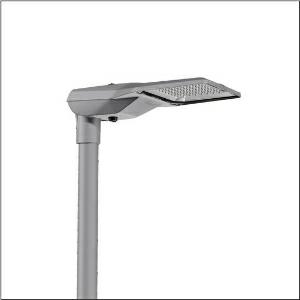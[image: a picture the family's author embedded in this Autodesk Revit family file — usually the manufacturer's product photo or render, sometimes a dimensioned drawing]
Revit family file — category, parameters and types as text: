
# Revit family: streetlight_sl_21_midi___p0_5a_5xe3v33t08nb_a5b7
name_source: partatom
category: Lighting Fixtures
units: mm (PartAtom-declared; Revit-internal decimal feet)

## family parameters
Cut with Voids When Loaded = No
Host = Face
Light Source = No
Part Type = Normal
Room Calculation Point = No
Round Connector Dimension = Use Diameter
Shared = No

## types (1)
- --- (1 x LED, 22310 lm, 151.2 W, 3000K)
    Apparent Load = 151 VA
    CIE Flux Codes = 37 73 96 100 100
    Color Rendering = 70
    Color Temperature = 3000K
    Default Elevation = 1800 mm
    Description = Streetlight SL 21 midi, mast luminaire, primary light control with lens, of PMMA, primary optical cover: cover, of toughened safety glass, transparent, light distribution: P0.5a, light emission: direct distribution, primary light characteristic: asymmetric, installation type: post-top, side-entry, LED, High Power LED, rated luminous flux: 22.310lm, luminous efficacy: 148lm/W, light colour: 730, colour temperature: 3000K, control gear: D4i, control: overheat protection, constant luminous flux control, time-dependent luminous flux control, flexible luminous flux parameterisation, pre-setting: logarithmic dimming characteristic, mains connection: 230..240V, AC, 50/60Hz, start of lifetime: 151W, end of service life: 157W, reduction: 70W, luminaire housing, of diecast aluminium, powder-coated, Siteco® metallic grey (DB 702S), corrosivity category C5 mid according to DIN EN ISO 12944, multi-level sealing system, sealing non-destructively replaceable, inclination adjustable: 0°, 5°, 10°, 15°, please order mast flange separately, length: 644mm, width: 335mm, height: 110mm, mast flange for spigot size: 42mm (side-entry): 5XC10008XM4, 60/48mm (side-entry/post-top): 5XC10108XM2, 76/60mm (side-entry/post-top): 5XC10108XM1, mounting height: 4..8m, Smart Interface below and above, protection rating (complete): IP66, insulation class (complete): insulation class II (safety insulation), certification: CE, ENEC, ENEC+, VDE, impact resistance: IK10, permissible operating ambient temperature for outdoor applications: -40..+50°C, standard-compliant lighting for roads and squares, packaging unit: 1 piece

Light Distribution: P0.5a
    Height = 111 mm
    Lamp = 1 x LED
    Lamp Light Flux = 22310 lm
    Lamp Power = 151.2 W
    Lamp count = 1
    Length = 644 mm
    Luminous efficacy = 148 lm/W
    Manufacturer = Siteco
    ModVariant = No
    Model = 5XE3V33T08NB
    Number of Poles = 1
    OnlyDefault = Yes
    Power Factor = 1
    Product Name = Streetlight SL 21 midi | P0.5a
    Product group = mast luminaire | pylon top
    ProductGroupID = 6100
    Protection Class = Protection class II
    Protection Degree = IP 66
    RLX_Detail_Level = 1
    RLX_Emergency_Light_Flux = 0 lm
    RLX_Emergency_Type = 0
    RLX_Emergency_Type_DB = No
    RlxData = <blob elided: 26821 chars, md5=66f19bde>
    Socket = socket
    Standby Power = 0 W
    System Light Flux = 22310 lm
    System Power = 151 W
    Type Comments = factory setting: luminous flux: 100 % | dim-lin: 254 | 802 mA
    Type Image = l_1004304.jpg
    URL = http://relux.com
    VarID = @adj_069004
    Voltage = 0 V
    Weight = 0.00 kg
    Width = 336 mm

## geometry (parser evidence)
native form markers: Blend x4, Sweep x13
no freeform markers — native parametric forms only
